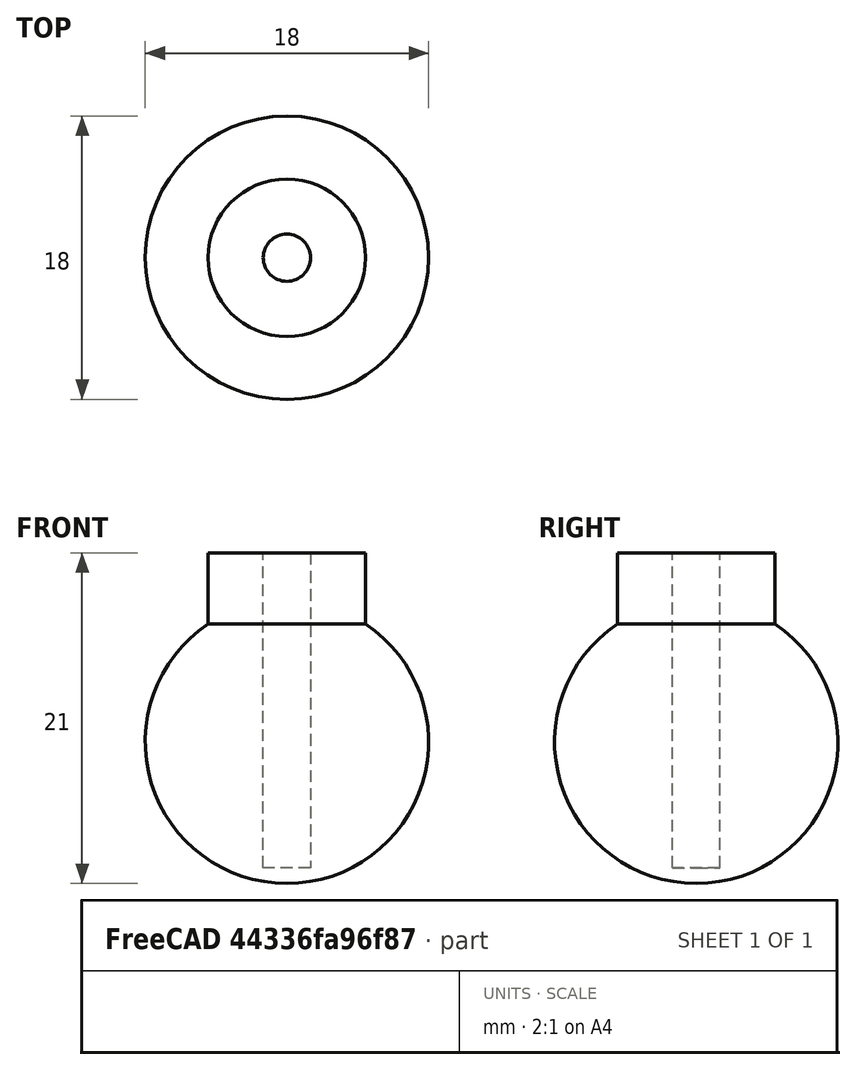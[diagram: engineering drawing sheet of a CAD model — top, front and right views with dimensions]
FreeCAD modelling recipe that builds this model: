
FCSTD DOCUMENT  (FreeCAD 0.15R4671 (Git))
Label: AP9 charging handle
License: All rights reserved
LicenseURL: http://en.wikipedia.org/wiki/All_rights_reserved
objects: Part::Cylinder×1, Part::Sphere×1, Part::MultiFuse×1, Sketcher::SketchObject×1, PartDesign::Pocket×1
note: 6 computed .brp shape members not serialized (recipe doc carries the construction recipe); baked Part::Feature solids carry a one-line shape summary decoded from their .brp

FEATURE [Part::Cylinder] Cylinder
  Angle = 360
  Height = 7
  Radius = 5
FEATURE [Part::Sphere] Sphere
  Angle1 = -90
  Angle2 = 90
  Angle3 = 360
  Placement = pos=(0,0,-5) rot=(0,0,1;0rad)
  Radius = 9
FEATURE [Part::MultiFuse] Fusion
  Shapes = -> [Cylinder,Sphere]
FEATURE [Sketcher::SketchObject] Sketch
  Placement = pos=(0,0,7) rot=(0,0,1;0rad)
  Support = -> Fusion [Face1]
  sketch-geometry (1):
    g0: Circle CenterX=0 CenterY=0 CenterZ=0 NormalX=0 NormalY=0 NormalZ=1 Radius=1.5
  constraints (2):
    c: Coincident(g0,g-1)
    c: Radius(g0) = 1.5
FEATURE [PartDesign::Pocket] Pocket
  Length = 20
  Sketch = -> Sketch
  Type = 0
